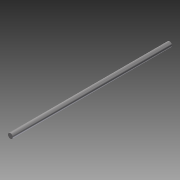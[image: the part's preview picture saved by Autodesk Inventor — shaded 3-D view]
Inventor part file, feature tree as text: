
AUTODESK INVENTOR PART (.ipt)
format: ipt  version: 2014 SP1 (Build 180222100, 222)  size: 82,432 bytes
history: native  units: mm
features: extrude x1, sketch x1
ambient origin geometry x8: Origin, YZ Plane, XZ Plane, XY Plane, X Axis, Y Axis, Z Axis, Center Point
bodies: Solid1 (feature_tree)
feature tree (2):
  extrude  "Extrusion1"  Depth=310.0mm TaperAngle=0.0deg
  sketch  "Sketch1"  dims[d0=9.525mm d1=310.0mm d2=0.0mm]
